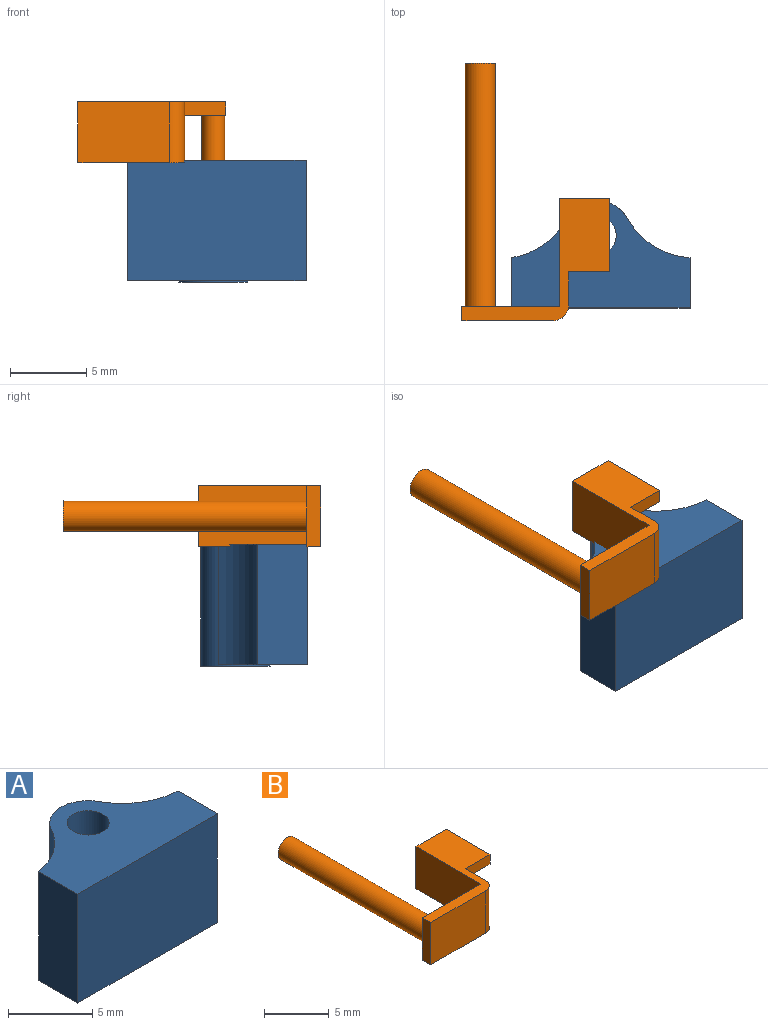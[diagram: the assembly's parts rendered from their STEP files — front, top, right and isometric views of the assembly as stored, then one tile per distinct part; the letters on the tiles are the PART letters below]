
ASSEMBLY  parts=2 mates=1
PART A: 10 faces, bbox 11.7x7x8 mm
  f0: cylinder r=2.28mm len=8mm, axis (0,0,-1), area 39.9mm2, adj f2,f3,f7,f8,f9
  f1: cylinder r=1.25mm len=8mm, axis (0,0,-1), area 62.8mm2, adj f2,f3
  f2: plane 11.71x7.04mm, normal (0,0,1), area 53.6mm2, adj f0,f1,f4,f5,f6,f8,f9
  f3: plane 4.55x4.55mm, normal (0,0,-1), area 11.4mm2, adj f0,f1
  f4: plane 7.9x3.3mm, normal (-1,0,0), area 26.1mm2, adj f2,f5,f7,f8
  f5: plane 11.71x7.9mm, normal (0,-1,0), area 92.5mm2, adj f2,f4,f6,f7
  f6: plane 7.9x3.3mm, normal (1,0,0), area 26.1mm2, adj f2,f5,f7,f9
  f7: plane 11.71x5.86mm, normal (0,0,-1), area 42.2mm2, adj f0,f4,f5,f6,f8,f9
  f8: cylinder r=5mm len=7.9mm, axis (0,0,1), area 36.2mm2, adj f0,f2,f4,f7
  f9: cylinder r=5mm len=7.9mm, axis (0,0,-1), area 39.9mm2, adj f0,f2,f6,f7
PART B: 16 faces, bbox 9.7x16.9x6.8 mm
  f0: plane 6.4x4mm, normal (0,1,0), area 22.5mm2, adj f1,f3,f4,f5,f8
  f1: cylinder r=1mm len=16mm, axis (0,1,0), area 100.5mm2, adj f0,f2
  f2: plane 2x2mm, normal (0,1,0), area 3.1mm2, adj f1
  f3: plane 9.7x8mm, normal (0,0,1), area 23.3mm2, adj f0,f4,f6,f7,f8,f9,f10,f12
  f4: plane 4x0.9mm, normal (-1,0,0), area 3.6mm2, adj f0,f3,f5,f7
  f5: plane 8x7mm, normal (0,0,-1), area 10.3mm2, adj f0,f4,f6,f7,f8,f9,f10
  f6: plane 7x4mm, normal (1,0,0), area 23.6mm2, adj f3,f5,f9,f10,f11,f12
  f7: plane 6x4mm, normal (0,-1,0), area 24mm2, adj f3,f4,f5,f10
  f8: plane 7.1x4mm, normal (-1,0,0), area 28.4mm2, adj f0,f3,f5,f9
  f9: plane 4x3.3mm, normal (0,1,0), area 4.9mm2, adj f3,f5,f6,f8,f11,f13
  f10: cylinder r=1mm len=4mm, axis (0,0,-1), area 6.3mm2, adj f3,f5,f6,f7
  f11: plane 4.8x2.7mm, normal (0,0,-1), area 11.2mm2, adj f6,f9,f12,f13,f14
  f12: plane 2.7x0.91mm, normal (0,-1,0), area 2.5mm2, adj f3,f6,f11,f13
  f13: plane 4.8x0.91mm, normal (1,0,0), area 4.4mm2, adj f3,f9,f11,f12
  f14: cylinder r=0.75mm len=5.9mm, axis (0,0,1), area 27.8mm2, adj f11,f15
  f15: plane 1.5x1.5mm, normal (0,0,-1), area 1.8mm2, adj f14
PLACE A t=(3.34,-3.18,-7.28)mm
PLACE B t=(-4.34,8.11,2.58)mm
MATE slider A.f1 <-> B.f14  axis (0,0,-1) through (3.34,-3.18,0.72)mm
